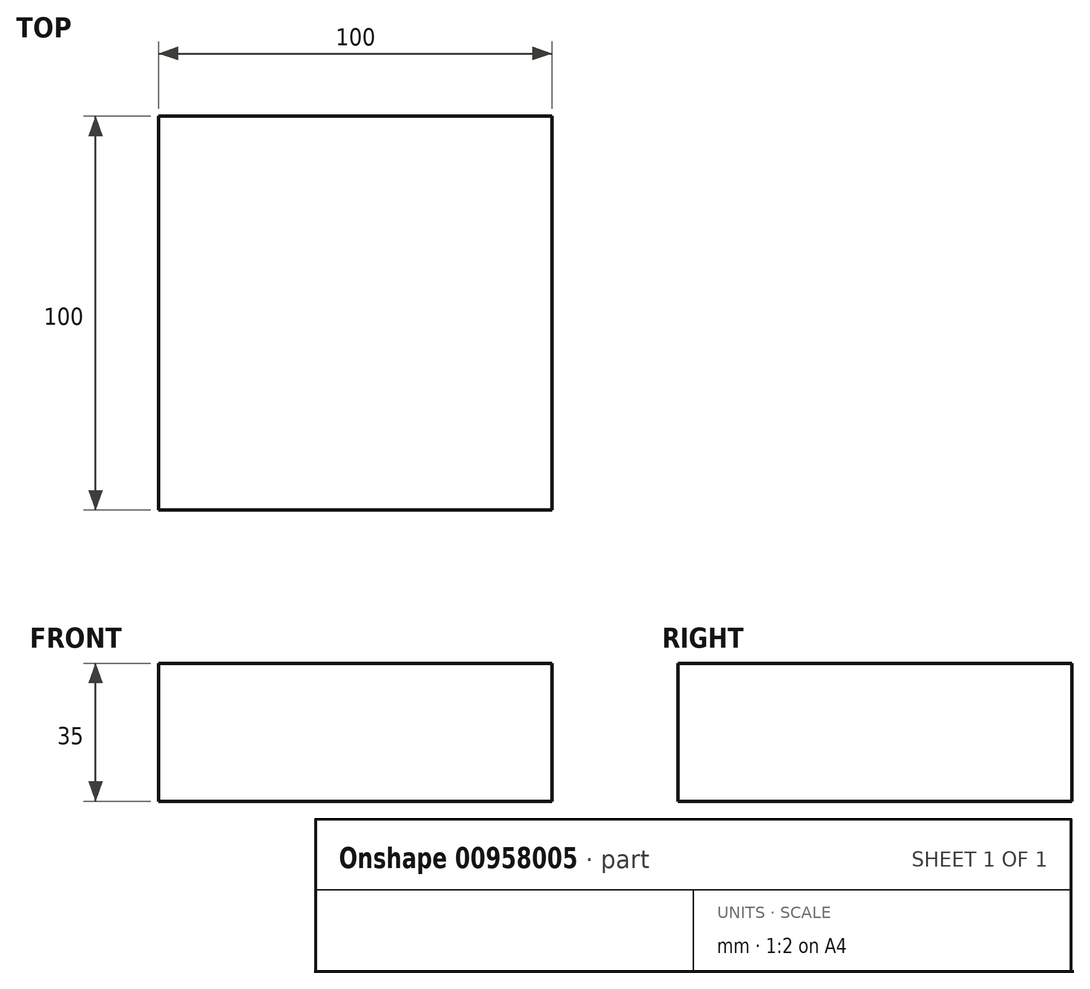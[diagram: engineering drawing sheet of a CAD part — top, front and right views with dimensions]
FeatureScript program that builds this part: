
annotation { "Feature Type Name" : "Feature", "Feature Type Description" : "" }
export const myFeature = defineFeature(function(context is Context, id is Id, definition is map)
    precondition{}
    {
        {
            var Q0;
            Q0=qCreatedBy(makeId("Top.planeOp"),FACE);
            var sketch = newSketch(context, id + "F0", { "sketchPlane" : qUnion([Q0])});
            skLineSegment(sketch, "E0.bottom", {"start": v(-50, 50) * mm, "end": v(50, 50) * mm});
            skLineSegment(sketch, "E0.top", {"start": v(-50, -50) * mm, "end": v(50, -50) * mm});
            skLineSegment(sketch, "E0.left", {"start": v(-50, 50) * mm, "end": v(-50, -50) * mm});
            skLineSegment(sketch, "E0.right", {"start": v(50, 50) * mm, "end": v(50, -50) * mm});
            skLineSegment(sketch, "E1", {"start": v(-50, 50) * mm, "end": v(50, -50) * mm, "construction": true});
            skLineSegment(sketch, "E2", {"start": v(-50, -50) * mm, "end": v(50, 50) * mm, "construction": true});
            skSolve(sketch);
        }
        {
            var Q0;
            Q0 = qSketchRegion(id + "F0", true);
            extrude(context, id + "F1", {"entities" : qUnion([Q0]), "oppositeDirection" : true, "depth" : 35 * mm, "offsetDistance" : 25.4 * mm});
        }
    });
